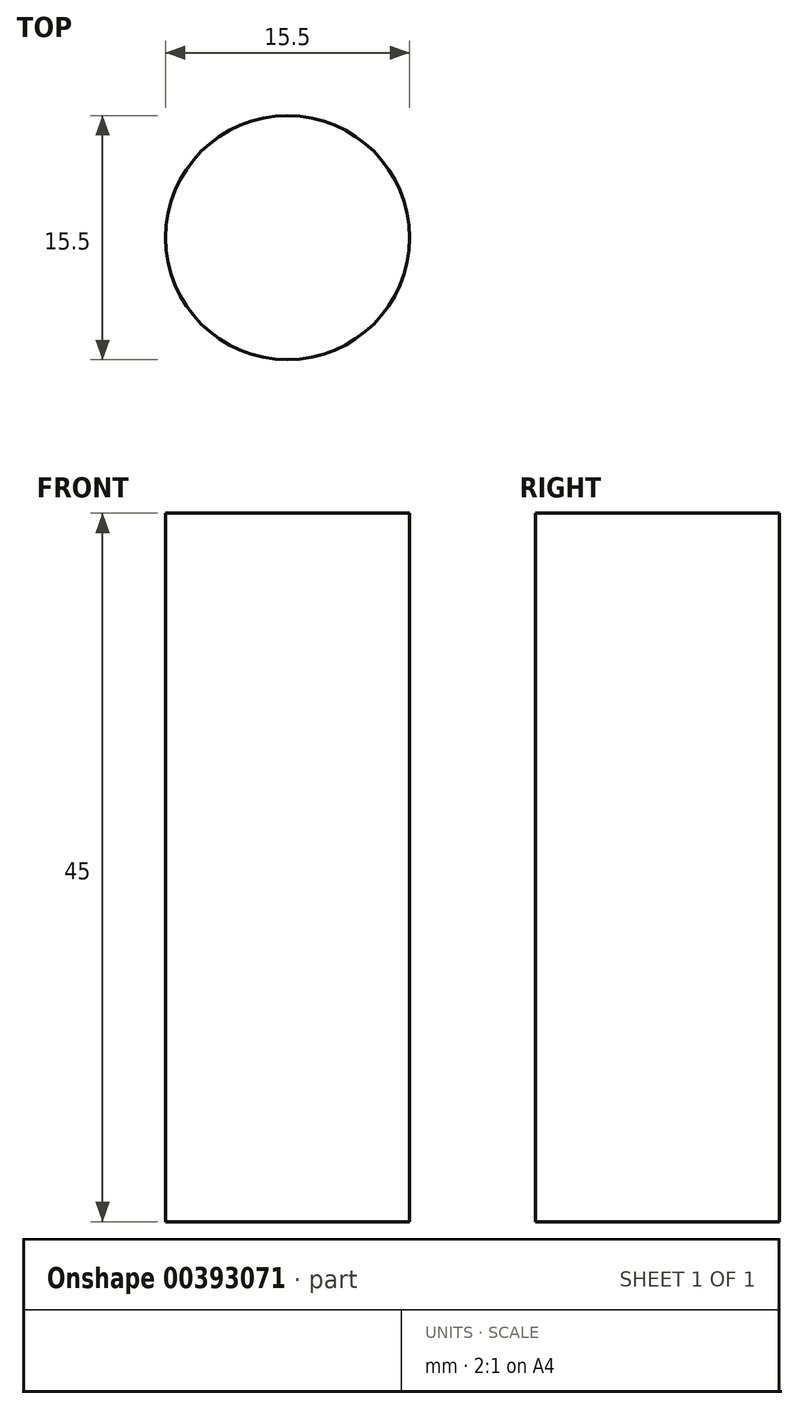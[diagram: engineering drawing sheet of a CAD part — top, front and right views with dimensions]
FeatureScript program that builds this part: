
annotation { "Feature Type Name" : "Feature", "Feature Type Description" : "" }
export const myFeature = defineFeature(function(context is Context, id is Id, definition is map)
    precondition{}
    {
        {
            var Q0;
            Q0=qCreatedBy(makeId("Top.planeOp"),FACE);
            var sketch = newSketch(context, id + "F0", { "sketchPlane" : qUnion([Q0])});
            skCircle(sketch, "E0", {"center": v(0, 0) * mm, "radius": 7.75 * mm});
            skSolve(sketch);
        }
        {
            var Q0;
            Q0=makeQuery(id+"F0.imprint","IMPRINT",FACE,{"disambiguationData":[TD([[makeQuery(id+"F0.imprint","IMPRINT",EDGE,{"derivedFrom":sQuery(id+"F0.wireOp",EDGE,"E0")}),1.0]])]});
            extrude(context, id + "F1", {"entities" : qUnion([Q0]), "depth" : 45 * mm});
        }
    });
